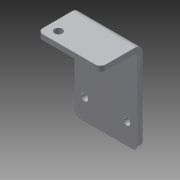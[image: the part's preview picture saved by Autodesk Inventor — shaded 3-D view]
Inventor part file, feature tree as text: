
AUTODESK INVENTOR PART (.ipt)
format: ipt  version: 2014 (Build 180170000, 170)  size: 122,368 bytes
history: native  units: in
note: dims shown in document units (in); Inventor stores cm internally (conversion verified against a paired STEP export)
features: sheet_metal_op x4, sketch x3, other x3, fillet x1
ambient origin geometry x8: Origin, YZ Plane, XZ Plane, XY Plane, X Axis, Y Axis, Z Axis, Center Point
bodies: Solid1 (feature_tree)
feature tree (11):
  sheet_metal_op  "Face1"
  sheet_metal_op  "Flange1"
  fillet  "Fillet1"  Radius=1.5in
  sketch  "Sketch1"  dims[d1=2.0in]
  other  "Plate1"
  sketch  "Sketch2"  dims[d2=0.163in]
  other  "Plate2"
  sheet_metal_op  "Bend1"
  sheet_metal_op  "Corner1"
  sketch  "Sketch4"  dims[d3=0.25in d4=0.7874in d6=1.0in d7=0.3937in d9=1.0in d11=0.125in d12=0.125in d13=0.0625in d14=0.25in d15=0.125in d16=1.0in d17=90.0deg d18=0.05in d19=0.5in d20=0.125in d21=0.125in d22=0.5in d28=0.187in d29=0.25in d30=1.25in d31=0.125in d32=0.0in d33=0.125in]
  other  "Cut2"
